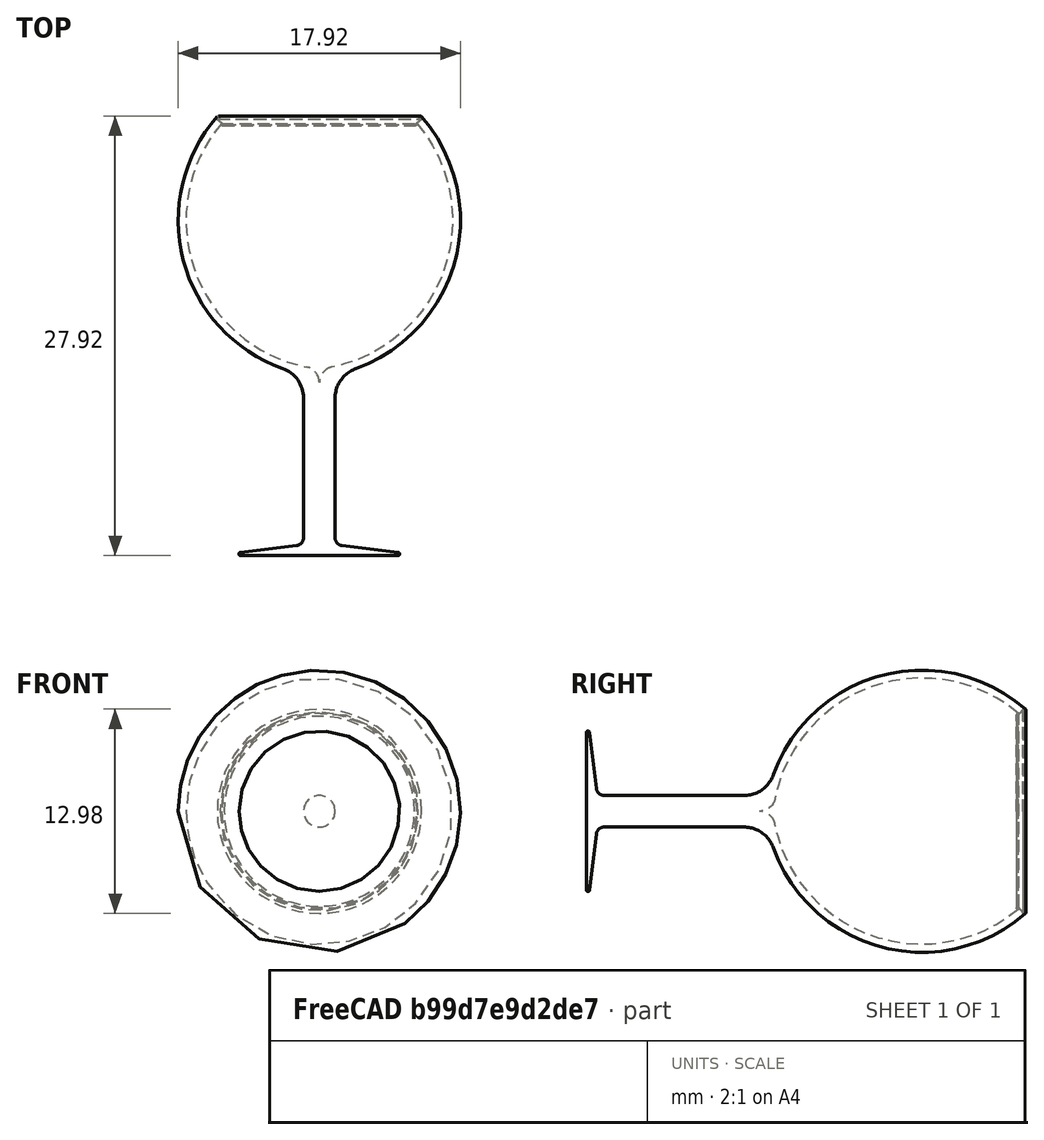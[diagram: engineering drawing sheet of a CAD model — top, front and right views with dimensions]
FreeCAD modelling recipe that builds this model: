
FCSTD DOCUMENT  (FreeCAD 0.16R6712 (Git))
Label: glass
License: All rights reserved
LicenseURL: http://en.wikipedia.org/wiki/All_rights_reserved
objects: Mesh::Feature×2, Sketcher::SketchObject×1, PartDesign::Revolution×1
note: 3 computed .brp shape members not serialized (recipe doc carries the construction recipe); baked Part::Feature solids carry a one-line shape summary decoded from their .brp

FEATURE [Sketcher::SketchObject] Sketch
  sketch-geometry (13):
    g0: LineSegment StartX=0 StartY=0 StartZ=0 EndX=-5 EndY=0 EndZ=0
    g1: LineSegment StartX=-5.01219 StartY=0.199255 StartZ=0 EndX=-1.43907 EndY=0.637979 EndZ=0
    g2: LineSegment StartX=-1 StartY=1.13425 StartZ=0 EndX=-1 EndY=10 EndZ=0
    g3: ArcOfCircle CenterX=1.03727 CenterY=21.3005 CenterZ=0 NormalX=0 NormalY=0 NormalZ=1 Radius=10 StartAngle=2.42305 EndAngle=4.36926
    g4: ArcOfCircle CenterX=-5 CenterY=0.1 CenterZ=0 NormalX=0 NormalY=0 NormalZ=1 Radius=0.1 StartAngle=1.69297 EndAngle=4.71239
    g5: ArcOfCircle CenterX=-1.5 CenterY=1.13425 CenterZ=0 NormalX=0 NormalY=0 NormalZ=1 Radius=0.5 StartAngle=4.83456 EndAngle=6.28319
    g6: ArcOfCircle CenterX=-3 CenterY=10 CenterZ=0 NormalX=0 NormalY=0 NormalZ=1 Radius=2 StartAngle=6.28319 EndAngle=7.51085
    g7: ArcOfCircle CenterX=1.03727 CenterY=21.3005 CenterZ=0 NormalX=0 NormalY=0 NormalZ=1 Radius=9.5 StartAngle=2.44006 EndAngle=4.51712
    g8: LineSegment StartX=0 StartY=11 StartZ=0 EndX=0 EndY=0 EndZ=0
    g9: LineSegment StartX=-6.48021 StartY=27.7415 StartZ=0 EndX=-6.0369 EndY=27.3617 EndZ=0
    g10: ArcOfCircle CenterX=-6.41514 CenterY=27.8175 CenterZ=0 NormalX=0 NormalY=0 NormalZ=1 Radius=0.1 StartAngle=4.00395 EndAngle=8.70624
    g11: ArcOfCircle CenterX=-6.12045 CenterY=27.4167 CenterZ=0 NormalX=0 NormalY=0 NormalZ=1 Radius=0.1 StartAngle=2.99085 EndAngle=5.70135
    g12: ArcOfCircle CenterX=-1 CenterY=11 CenterZ=0 NormalX=0 NormalY=0 NormalZ=1 Radius=1 StartAngle=5.39508e-07 EndAngle=1.37553
  constraints (38):
    c: Coincident(g0,g-1)
    c: Horizontal(g0)
    c: Vertical(g2)
    c: Radius(g3) = 10
    c: Tangent(g0,g4) = 1.5708
    c: Tangent(g1,g4) = 1.5708
    c: Radius(g4) = 0.1
    c: Tangent(g1,g5) = -1.5708
    c: Tangent(g2,g5) = -1.5708
    c: Radius(g6) = 2
    c: Tangent(g2,g6)
    c: Tangent(g3,g6)
    c: Coincident(g2,g6)
    c: Coincident(g3,g6)
    c: Radius(g5) = 0.5
    c: Radius(g7) = 9.5
    c: Coincident(g8,g-1)
    c: Tangent(g9,g10)
    c: Tangent(g3,g10)
    c: Coincident(g9,g10)
    c: Coincident(g3,g10)
    c: Radius(g10) = 0.1
    c: Coincident(g7,g11)
    c: Coincident(g11,g9)
    c: Equal(g11,g10)
    c: Perpendicular(g7,g9)
    c: Angle(g0,g1) = 0.122173
    c: Coincident(g12,g8)
    c: Coincident(g12,g7)
    c: Tangent(g7,g12)
    c: Tangent(g12,g8)
    c: Coincident(g7,g3)
    c: Vertical(g8)
    c: Radius(g12) = 1
    c: DistanceX(g-2,g4) = -5
    c: DistanceY(g-1,g2) = 10
    c: Distance(g2,g8) = 1
    c: DistanceY(g-1,g12) = 11
FEATURE [PartDesign::Revolution] Revolution
  Angle = 360
  Axis = (0,1,0)
  Base = (0,0,0)
  ReferenceAxis = -> Sketch [V_Axis]
  Sketch = -> Sketch
FEATURE [Mesh::Feature] Mesh001  label="Revolution (Meshed)"
FEATURE [Mesh::Feature] Mesh  label="glass"
  Placement = pos=(40,-3.5,30) rot=(0,0,1;0rad)
